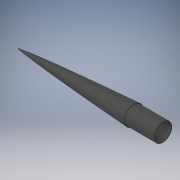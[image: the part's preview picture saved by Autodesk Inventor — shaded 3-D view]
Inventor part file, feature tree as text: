
AUTODESK INVENTOR PART (.ipt)
format: ipt  version: 2017 SP1 (Build 210196100, 196)  size: 163,328 bytes
history: native  units: in
note: dims shown in document units (in); Inventor stores cm internally (conversion verified against a paired STEP export)
features: sketch x2, revolve x1, shell x1, extrude x1, other x1
ambient origin geometry x8: Origin, YZ Plane, XZ Plane, XY Plane, X Axis, Y Axis, Z Axis, Center Point
bodies: Solid1 (feature_tree)
feature tree (6):
  revolve  "Revolution1"  [1 undecoded]
  shell  "Shell1"  Thickness=90.0deg
  extrude  "Extrusion1"  Depth=12.0in
  sketch  "Sketch1"  dims[d0=0.0in d1=18.8976in d3=4.0in d4=90.0deg]
  other  "2D Equation Curve1"
  sketch  "Sketch2"  dims[d5=0.25in d6=7.5in d7=7.0in d8=12.0in d9=0.0in]
note: 1 required parameter value undecoded (feature->parameter linkage not recoverable at this tier; creation-order binding heuristic only, values carry confidence <= 0.55)
